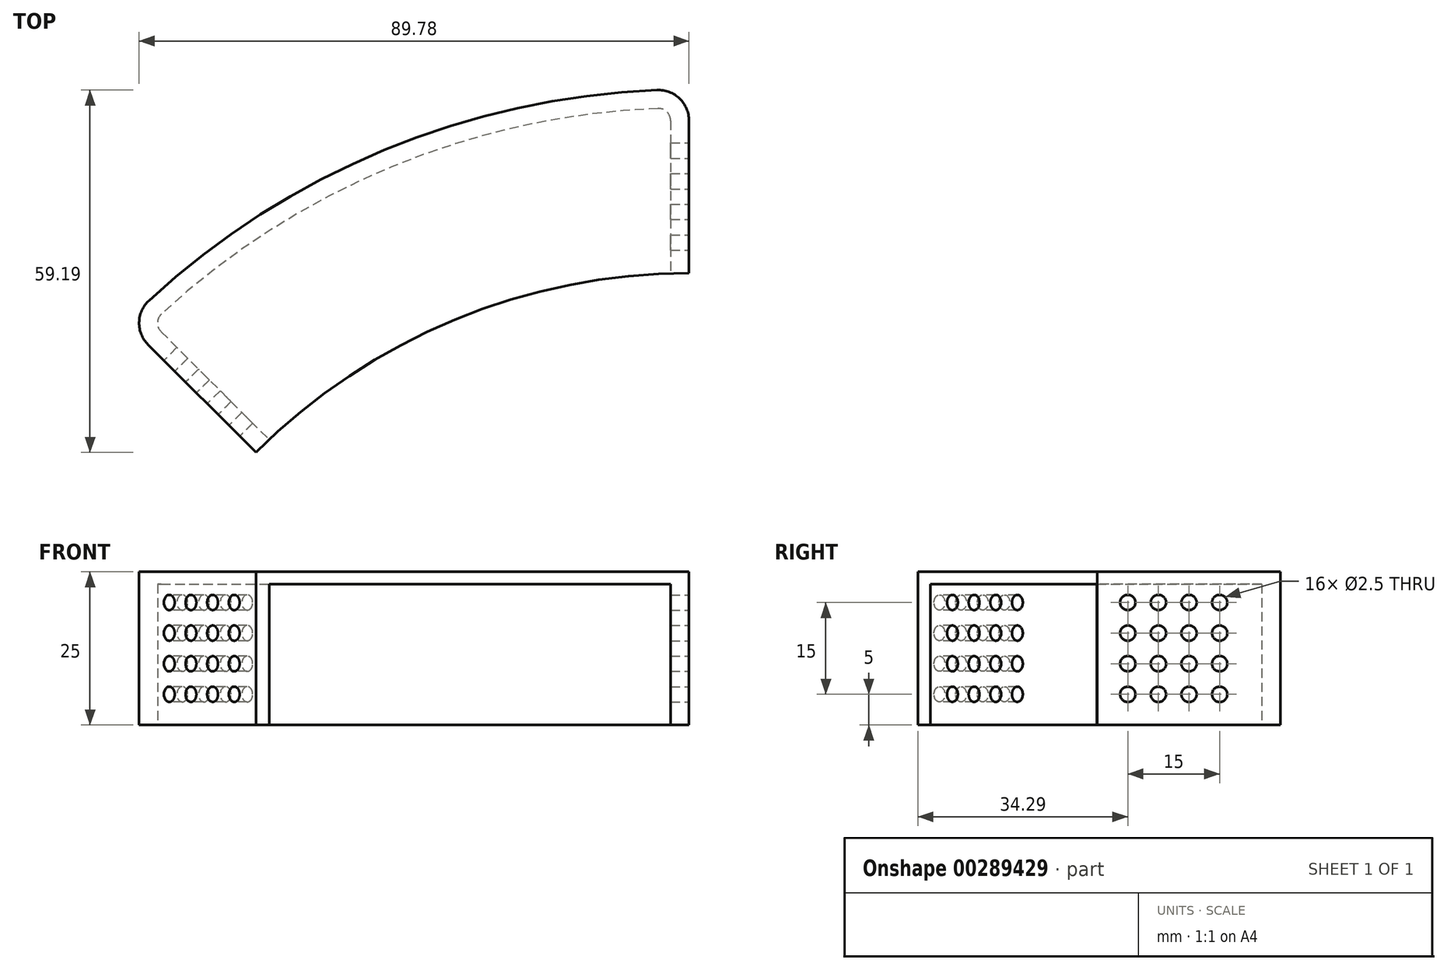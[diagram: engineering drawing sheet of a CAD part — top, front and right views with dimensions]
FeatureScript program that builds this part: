
annotation { "Feature Type Name" : "Feature", "Feature Type Description" : "" }
export const myFeature = defineFeature(function(context is Context, id is Id, definition is map)
    precondition{}
    {
        {
            var Q0;
            Q0=qCreatedBy(makeId("Top.planeOp"),FACE);
            var sketch = newSketch(context, id + "F0", { "sketchPlane" : qUnion([Q0])});
            skArc(sketch, "E0", {"start": v(0, 100) * mm, "mid": v(-38.27, 92.39) * mm, "end": v(-70.71, 70.71) * mm});
            skArc(sketch, "E1", {"start": v(-5.2, 129.9) * mm, "mid": v(-49.75, 120.1) * mm, "end": v(-88.17, 95.53) * mm});
            skLineSegment(sketch, "E2", {"start": v(0, 100) * mm, "end": v(0, 124.9) * mm});
            skLineSegment(sketch, "E3", {"start": v(-70.71, 70.71) * mm, "end": v(-88.32, 88.32) * mm});
            skPoint(sketch, "E4.visualSharp", {"position": v(-91.92, 91.92) * mm});
            skArc(sketch, "E4.filletArc", {"start": v(-88.17, 95.53) * mm, "mid": v(-89.78, 91.95) * mm, "end": v(-88.32, 88.32) * mm});
            skPoint(sketch, "E5.visualSharp", {"position": v(0, 130) * mm});
            skArc(sketch, "E5.filletArc", {"start": v(0, 124.9) * mm, "mid": v(-1.54, 128.5) * mm, "end": v(-5.2, 129.9) * mm});
            skSolve(sketch);
        }
        {
            var Q0;
            Q0=makeQuery(id+"F0.imprint","IMPRINT",FACE,{"disambiguationData":[TD([[makeQuery(id+"F0.imprint","IMPRINT",EDGE,{"derivedFrom":sQuery(id+"F0.wireOp",EDGE,"E0")}),-1.0]])]});
            extrude(context, id + "F1", {"entities" : qUnion([Q0]), "depth" : 25 * mm});
        }
        {
            var Q0;
            Q0=makeQuery(id+"F1.opExtrude","CAP_FACE",FACE,{"disambiguationData":[OSD([sQuery(id+"F0.wireOp",EDGE,"E0"),sQuery(id+"F0.wireOp",EDGE,"E1"),sQuery(id+"F0.wireOp",EDGE,"E2"),sQuery(id+"F0.wireOp",EDGE,"E3"),sQuery(id+"F0.wireOp",EDGE,"E4.filletArc"),sQuery(id+"F0.wireOp",EDGE,"E5.filletArc")])],"isStart":true});
            var sketch = newSketch(context, id + "F2", { "sketchPlane" : qUnion([Q0])});
            skArc(sketch, "E6.0", {"start": v(-86.14, -93.32) * mm, "mid": v(-48.6, -117.33) * mm, "end": v(-5.08, -126.9) * mm});
            skLineSegment(sketch, "E6.1", {"start": v(-3, -124.9) * mm, "end": v(-3, -102.96) * mm});
            skArc(sketch, "E6.3", {"start": v(-5.08, -126.9) * mm, "mid": v(-3.61, -126.34) * mm, "end": v(-3, -124.9) * mm});
            skLineSegment(sketch, "E6.4", {"start": v(-70.68, -74.92) * mm, "end": v(-86.2, -90.44) * mm});
            skArc(sketch, "E6.5", {"start": v(-86.2, -90.44) * mm, "mid": v(-86.78, -91.9) * mm, "end": v(-86.14, -93.32) * mm});
            skLineSegment(sketch, "E7", {"start": v(-70.68, -74.92) * mm, "end": v(-68.56, -72.8) * mm});
            skLineSegment(sketch, "E8", {"start": v(-3, -102.96) * mm, "end": v(-3, -99.95) * mm});
            skArc(sketch, "E9", {"start": v(-68.56, -72.8) * mm, "mid": v(-38.27, -92.39) * mm, "end": v(-3, -99.95) * mm});
            skSolve(sketch);
        }
        {
            var Q0;
            Q0 = qSketchRegion(id + "F2", true);
            extrude(context, id + "F3", {"entities" : qUnion([Q0]), "operationType" : NewBodyOperationType.REMOVE, "oppositeDirection" : true, "depth" : 23 * mm});
        }
        {
            var Q0;
            Q0=makeQuery(id+"F1.opExtrude","SWEPT_FACE",FACE,{"disambiguationData":[OSD([sQuery(id+"F0.wireOp",EDGE,"E3")])]});
            var sketch = newSketch(context, id + "F4", { "sketchPlane" : qUnion([Q0])});
            skCircle(sketch, "E10", {"center": v(-105, 20) * mm, "radius": 1.25 * mm});
            skCircle(sketch, "E11.0.1.0", {"center": v(-105, 15) * mm, "radius": 1.25 * mm});
            skCircle(sketch, "E11.0.2.0", {"center": v(-105, 10) * mm, "radius": 1.25 * mm});
            skCircle(sketch, "E11.0.3.0", {"center": v(-105, 5) * mm, "radius": 1.25 * mm});
            skCircle(sketch, "E11.1.0.0", {"center": v(-110, 20) * mm, "radius": 1.25 * mm});
            skCircle(sketch, "E11.1.1.0", {"center": v(-110, 15) * mm, "radius": 1.25 * mm});
            skCircle(sketch, "E11.1.2.0", {"center": v(-110, 10) * mm, "radius": 1.25 * mm});
            skCircle(sketch, "E11.1.3.0", {"center": v(-110, 5) * mm, "radius": 1.25 * mm});
            skCircle(sketch, "E11.2.0.0", {"center": v(-115, 20) * mm, "radius": 1.25 * mm});
            skCircle(sketch, "E11.2.1.0", {"center": v(-115, 15) * mm, "radius": 1.25 * mm});
            skCircle(sketch, "E11.2.2.0", {"center": v(-115, 10) * mm, "radius": 1.25 * mm});
            skCircle(sketch, "E11.2.3.0", {"center": v(-115, 5) * mm, "radius": 1.25 * mm});
            skCircle(sketch, "E11.3.0.0", {"center": v(-120, 20) * mm, "radius": 1.25 * mm});
            skCircle(sketch, "E11.3.1.0", {"center": v(-120, 15) * mm, "radius": 1.25 * mm});
            skCircle(sketch, "E11.3.2.0", {"center": v(-120, 10) * mm, "radius": 1.25 * mm});
            skCircle(sketch, "E11.3.3.0", {"center": v(-120, 5) * mm, "radius": 1.25 * mm});
            skLineSegment(sketch, "E11.direction1", {"start": v(-105, 20) * mm, "end": v(-110, 20) * mm, "construction": true});
            skLineSegment(sketch, "E11.direction2", {"start": v(-105, 20) * mm, "end": v(-105, 15) * mm, "construction": true});
            skSolve(sketch);
        }
        {
            var Q0;
            Q0 = qSketchRegion(id + "F4", true);
            extrude(context, id + "F5", {"entities" : qUnion([Q0]), "operationType" : NewBodyOperationType.REMOVE, "oppositeDirection" : true, "depth" : 3 * mm});
        }
        {
            var Q0;
            Q0=makeQuery(id+"F1.opExtrude","SWEPT_FACE",FACE,{"disambiguationData":[OSD([sQuery(id+"F0.wireOp",EDGE,"E2")])]});
            var sketch = newSketch(context, id + "F6", { "sketchPlane" : qUnion([Q0])});
            skCircle(sketch, "E12", {"center": v(105, 20) * mm, "radius": 1.25 * mm});
            skCircle(sketch, "E13.0.1.0", {"center": v(105, 15) * mm, "radius": 1.25 * mm});
            skCircle(sketch, "E13.0.2.0", {"center": v(105, 10) * mm, "radius": 1.25 * mm});
            skCircle(sketch, "E13.0.3.0", {"center": v(105, 5) * mm, "radius": 1.25 * mm});
            skCircle(sketch, "E13.1.0.0", {"center": v(110, 20) * mm, "radius": 1.25 * mm});
            skCircle(sketch, "E13.1.1.0", {"center": v(110, 15) * mm, "radius": 1.25 * mm});
            skCircle(sketch, "E13.1.2.0", {"center": v(110, 10) * mm, "radius": 1.25 * mm});
            skCircle(sketch, "E13.1.3.0", {"center": v(110, 5) * mm, "radius": 1.25 * mm});
            skCircle(sketch, "E13.2.0.0", {"center": v(115, 20) * mm, "radius": 1.25 * mm});
            skCircle(sketch, "E13.2.1.0", {"center": v(115, 15) * mm, "radius": 1.25 * mm});
            skCircle(sketch, "E13.2.2.0", {"center": v(115, 10) * mm, "radius": 1.25 * mm});
            skCircle(sketch, "E13.2.3.0", {"center": v(115, 5) * mm, "radius": 1.25 * mm});
            skCircle(sketch, "E13.3.0.0", {"center": v(120, 20) * mm, "radius": 1.25 * mm});
            skCircle(sketch, "E13.3.1.0", {"center": v(120, 15) * mm, "radius": 1.25 * mm});
            skCircle(sketch, "E13.3.2.0", {"center": v(120, 10) * mm, "radius": 1.25 * mm});
            skCircle(sketch, "E13.3.3.0", {"center": v(120, 5) * mm, "radius": 1.25 * mm});
            skLineSegment(sketch, "E13.direction1", {"start": v(105, 20) * mm, "end": v(110, 20) * mm, "construction": true});
            skLineSegment(sketch, "E13.direction2", {"start": v(105, 20) * mm, "end": v(105, 15) * mm, "construction": true});
            skSolve(sketch);
        }
        {
            var Q0;
            Q0 = qSketchRegion(id + "F6", true);
            extrude(context, id + "F7", {"entities" : qUnion([Q0]), "operationType" : NewBodyOperationType.REMOVE, "oppositeDirection" : true, "depth" : 3 * mm});
        }
    });
